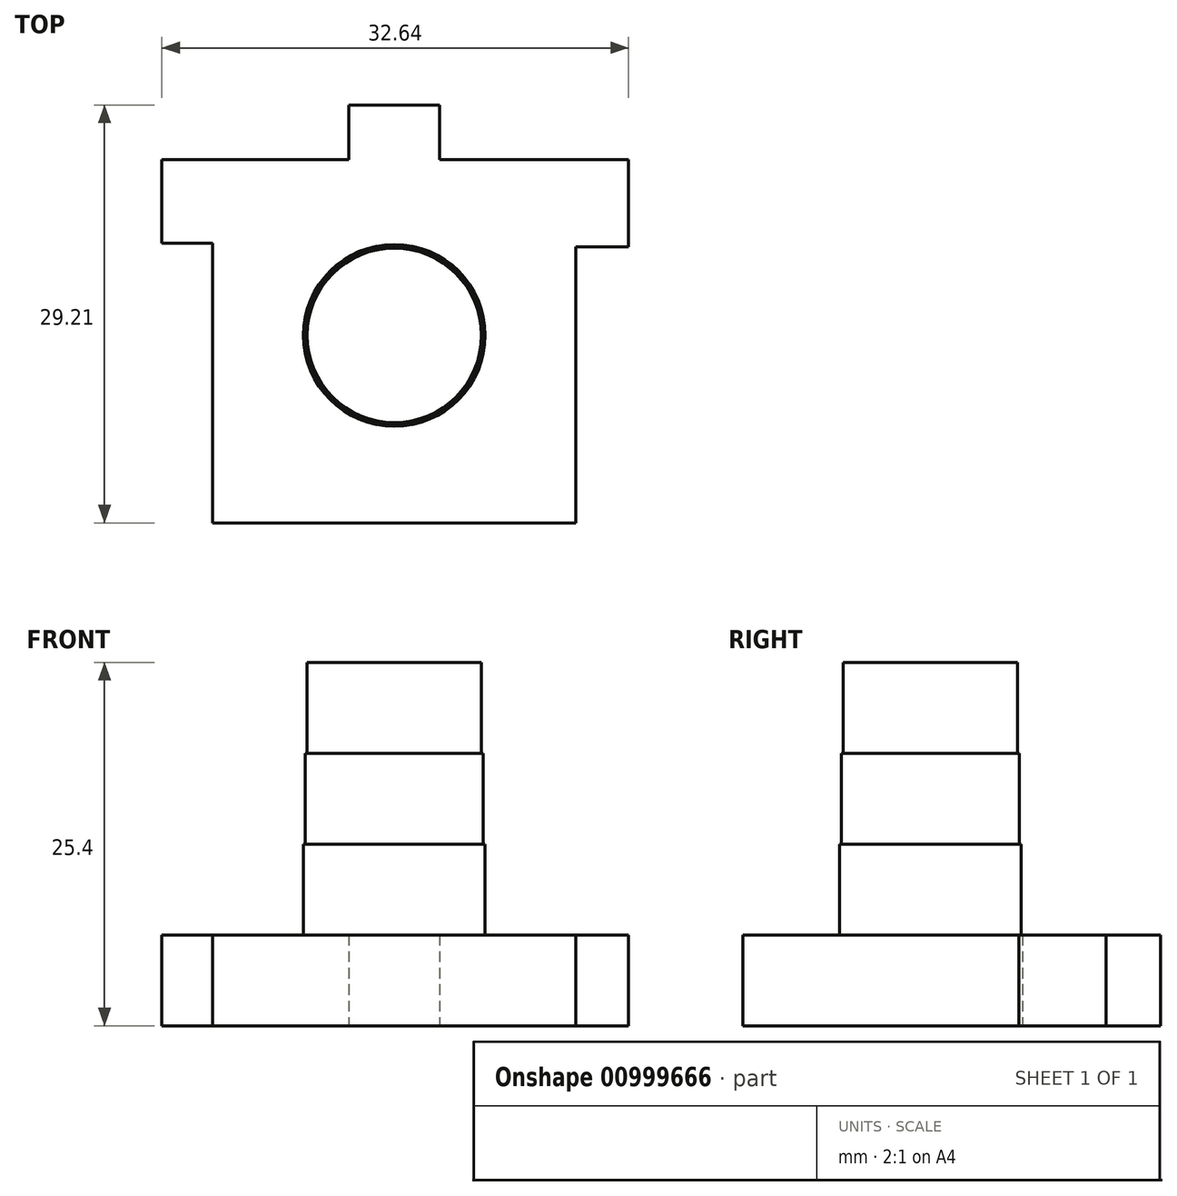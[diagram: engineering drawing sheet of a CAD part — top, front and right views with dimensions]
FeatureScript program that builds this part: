
annotation { "Feature Type Name" : "Feature", "Feature Type Description" : "" }
export const myFeature = defineFeature(function(context is Context, id is Id, definition is map)
    precondition{}
    {
        {
            var Q0;
            Q0=qCreatedBy(makeId("Top.planeOp"),FACE);
            var sketch = newSketch(context, id + "F0", { "sketchPlane" : qUnion([Q0])});
            skLineSegment(sketch, "E0.bottom", {"start": v(0, 0) * mm, "end": v(25.4, 0) * mm});
            skLineSegment(sketch, "E0.top", {"start": v(0, 25.4) * mm, "end": v(25.4, 25.4) * mm});
            skLineSegment(sketch, "E0.left", {"start": v(0, 0) * mm, "end": v(0, 25.4) * mm});
            skLineSegment(sketch, "E0.right", {"start": v(25.4, 0) * mm, "end": v(25.4, 25.4) * mm});
            skLineSegment(sketch, "E1.bottom", {"start": v(9.52, 25.4) * mm, "end": v(15.87, 25.4) * mm});
            skLineSegment(sketch, "E1.top", {"start": v(9.52, 29.21) * mm, "end": v(15.87, 29.21) * mm});
            skLineSegment(sketch, "E1.left", {"start": v(9.52, 25.4) * mm, "end": v(9.52, 29.21) * mm});
            skLineSegment(sketch, "E1.right", {"start": v(15.87, 25.4) * mm, "end": v(15.87, 29.21) * mm});
            skLineSegment(sketch, "E2.bottom", {"start": v(25.4, 25.4) * mm, "end": v(29.08, 25.4) * mm});
            skLineSegment(sketch, "E2.top", {"start": v(25.4, 19.3) * mm, "end": v(29.08, 19.3) * mm});
            skLineSegment(sketch, "E2.left", {"start": v(25.4, 25.4) * mm, "end": v(25.4, 19.3) * mm});
            skLineSegment(sketch, "E2.right", {"start": v(29.08, 25.4) * mm, "end": v(29.08, 19.3) * mm});
            skLineSegment(sketch, "E3.bottom", {"start": v(0, 25.4) * mm, "end": v(-3.56, 25.4) * mm});
            skLineSegment(sketch, "E3.top", {"start": v(0, 19.56) * mm, "end": v(-3.56, 19.56) * mm});
            skLineSegment(sketch, "E3.left", {"start": v(0, 25.4) * mm, "end": v(0, 19.56) * mm});
            skLineSegment(sketch, "E3.right", {"start": v(-3.56, 25.4) * mm, "end": v(-3.56, 19.56) * mm});
            skSolve(sketch);
        }
        {
            var Q0;
            Q0 = qSketchRegion(id + "F0", true);
            extrude(context, id + "F1", {"entities" : qUnion([Q0]), "depth" : 6.35 * mm, "offsetDistance" : 25.4 * mm});
        }
        {
            var Q0;
            Q0=makeQuery(id+"F1.opExtrude","CAP_FACE",FACE,{"disambiguationData":[OSD([sQuery(id+"F0.wireOp",EDGE,"E0.bottom"),sQuery(id+"F0.wireOp",EDGE,"E0.top"),sQuery(id+"F0.wireOp",EDGE,"E0.left"),sQuery(id+"F0.wireOp",EDGE,"E0.right"),sQuery(id+"F0.wireOp",EDGE,"E1.top"),sQuery(id+"F0.wireOp",EDGE,"E1.left"),sQuery(id+"F0.wireOp",EDGE,"E1.right"),sQuery(id+"F0.wireOp",EDGE,"E2.bottom"),sQuery(id+"F0.wireOp",EDGE,"E2.top"),sQuery(id+"F0.wireOp",EDGE,"E2.right"),sQuery(id+"F0.wireOp",EDGE,"E3.bottom"),sQuery(id+"F0.wireOp",EDGE,"E3.top"),sQuery(id+"F0.wireOp",EDGE,"E3.right")])],"isStart":false});
            var sketch = newSketch(context, id + "F2", { "sketchPlane" : qUnion([Q0])});
            skCircle(sketch, "E4", {"center": v(12.7, 13.1) * mm, "radius": 6.35 * mm});
            skPoint(sketch, "E4.centerSnap0", {"position": v(12.7, 0) * mm});
            skSolve(sketch);
        }
        {
            var Q0;
            Q0 = qSketchRegion(id + "F2", true);
            extrude(context, id + "F3", {"entities" : qUnion([Q0]), "operationType" : NewBodyOperationType.ADD, "depth" : 6.35 * mm, "offsetDistance" : 25.4 * mm});
        }
        {
            var Q0;
            Q0=makeQuery(id+"F3.opExtrude","CAP_FACE",FACE,{"disambiguationData":[OSD([sQuery(id+"F2.wireOp",EDGE,"E4")])],"isStart":false});
            var sketch = newSketch(context, id + "F4", { "sketchPlane" : qUnion([Q0])});
            skCircle(sketch, "E5", {"center": v(12.7, 13.1) * mm, "radius": 6.22 * mm});
            skSolve(sketch);
        }
        {
            var Q0;
            Q0 = qSketchRegion(id + "F4", true);
            extrude(context, id + "F5", {"entities" : qUnion([Q0]), "operationType" : NewBodyOperationType.ADD, "depth" : 6.35 * mm, "offsetDistance" : 25.4 * mm});
        }
        {
            var Q0;
            Q0=makeQuery(id+"F5.opExtrude","CAP_FACE",FACE,{"disambiguationData":[OSD([sQuery(id+"F4.wireOp",EDGE,"E5")])],"isStart":false});
            var sketch = newSketch(context, id + "F6", { "sketchPlane" : qUnion([Q0])});
            skCircle(sketch, "E6", {"center": v(12.7, 13.1) * mm, "radius": 6.1 * mm});
            skSolve(sketch);
        }
        {
            var Q0;
            Q0 = qSketchRegion(id + "F6", true);
            extrude(context, id + "F7", {"entities" : qUnion([Q0]), "operationType" : NewBodyOperationType.ADD, "depth" : 6.35 * mm, "offsetDistance" : 25.4 * mm});
        }
    });
